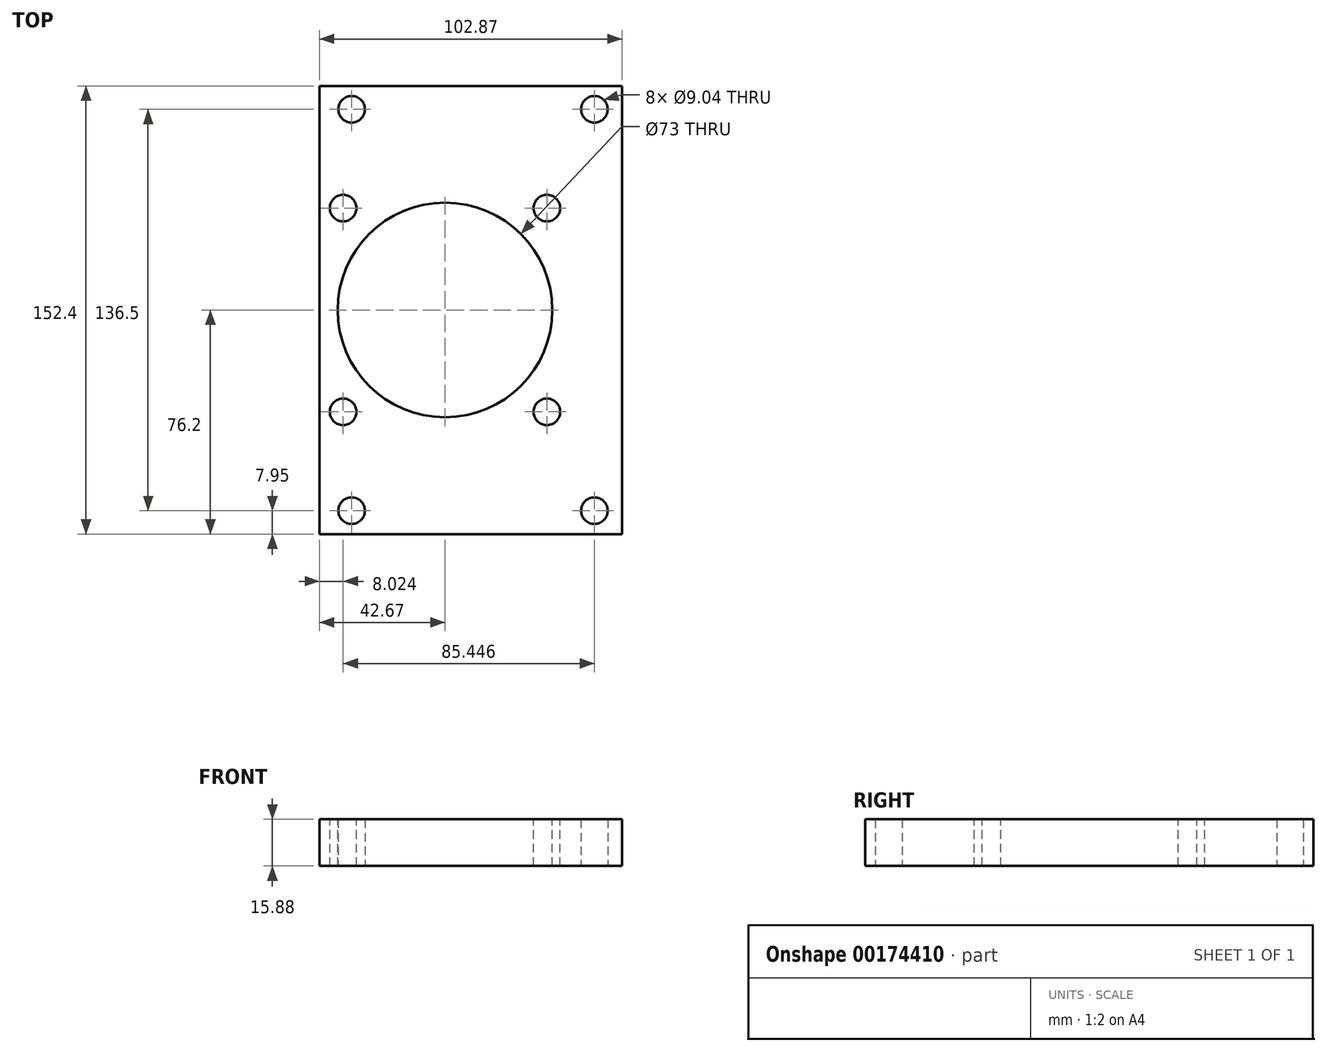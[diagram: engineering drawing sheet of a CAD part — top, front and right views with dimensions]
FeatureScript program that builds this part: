
annotation { "Feature Type Name" : "Feature", "Feature Type Description" : "" }
export const myFeature = defineFeature(function(context is Context, id is Id, definition is map)
    precondition{}
    {
        {
            var Q0;
            Q0=qCreatedBy(makeId("Top.planeOp"),FACE);
            var sketch = newSketch(context, id + "F0", { "sketchPlane" : qUnion([Q0])});
            skLineSegment(sketch, "E0.bottom", {"start": v(-42.67, 76.2) * mm, "end": v(60.2, 76.2) * mm});
            skLineSegment(sketch, "E0.top", {"start": v(-42.67, -76.2) * mm, "end": v(60.2, -76.2) * mm});
            skLineSegment(sketch, "E0.left", {"start": v(-42.67, 76.2) * mm, "end": v(-42.67, -76.2) * mm});
            skLineSegment(sketch, "E0.right", {"start": v(60.2, 76.2) * mm, "end": v(60.2, -76.2) * mm});
            skPoint(sketch, "E0.middle", {"position": v(8.76, 0) * mm});
            skCircle(sketch, "E1", {"center": v(-31.75, 68.25) * mm, "radius": 4.52 * mm});
            skCircle(sketch, "E2", {"center": v(50.8, 68.25) * mm, "radius": 4.52 * mm});
            skCircle(sketch, "E3", {"center": v(50.8, -68.25) * mm, "radius": 4.52 * mm});
            skCircle(sketch, "E4", {"center": v(-31.75, -68.25) * mm, "radius": 4.52 * mm});
            skSolve(sketch);
        }
        {
            var Q0;
            Q0=makeQuery(id+"F0.imprint","IMPRINT",FACE,{"disambiguationData":[TD([[makeQuery(id+"F0.imprint","IMPRINT",EDGE,{"derivedFrom":sQuery(id+"F0.wireOp",EDGE,"E0.bottom")}),-1.0]])]});
            extrude(context, id + "F1", {"entities" : qUnion([Q0]), "depth" : 15.88 * mm});
        }
        {
            var Q0;
            Q0 = qSketchRegion(id + "F0", true);
            extrude(context, id + "F2", {"entities" : qUnion([Q0]), "operationType" : NewBodyOperationType.REMOVE, "endBound" : BoundingType.THROUGH_ALL, "oppositeDirection" : true, "depth" : 25.4 * mm});
        }
        {
            var Q0;
            Q0=makeQuery(id+"F1.opExtrude","CAP_FACE",FACE,{"disambiguationData":[OSD([sQuery(id+"F0.wireOp",EDGE,"E0.bottom"),sQuery(id+"F0.wireOp",EDGE,"E0.top"),sQuery(id+"F0.wireOp",EDGE,"E0.left"),sQuery(id+"F0.wireOp",EDGE,"E0.right"),sQuery(id+"F0.wireOp",EDGE,"E1"),sQuery(id+"F0.wireOp",EDGE,"E2"),sQuery(id+"F0.wireOp",EDGE,"E3"),sQuery(id+"F0.wireOp",EDGE,"E4")])],"isStart":false});
            var sketch = newSketch(context, id + "F3", { "sketchPlane" : qUnion([Q0])});
            skCircle(sketch, "E5", {"center": v(0, 0) * mm, "radius": 36.5 * mm});
            skSolve(sketch);
        }
        {
            var Q0;
            Q0 = qSketchRegion(id + "F3", true);
            extrude(context, id + "F4", {"entities" : qUnion([Q0]), "operationType" : NewBodyOperationType.REMOVE, "endBound" : BoundingType.THROUGH_ALL, "oppositeDirection" : true, "depth" : 25.4 * mm});
        }
        {
            var Q0;
            Q0=makeQuery(id+"F1.opExtrude","CAP_FACE",FACE,{"disambiguationData":[OSD([sQuery(id+"F0.wireOp",EDGE,"E0.bottom"),sQuery(id+"F0.wireOp",EDGE,"E0.top"),sQuery(id+"F0.wireOp",EDGE,"E0.left"),sQuery(id+"F0.wireOp",EDGE,"E0.right"),sQuery(id+"F0.wireOp",EDGE,"E1"),sQuery(id+"F0.wireOp",EDGE,"E2"),sQuery(id+"F0.wireOp",EDGE,"E3"),sQuery(id+"F0.wireOp",EDGE,"E4")])],"isStart":false});
            var sketch = newSketch(context, id + "F5", { "sketchPlane" : qUnion([Q0])});
            skCircle(sketch, "E6", {"center": v(-34.65, 34.65) * mm, "radius": 4.52 * mm});
            skCircle(sketch, "E7", {"center": v(34.65, 34.65) * mm, "radius": 4.52 * mm});
            skCircle(sketch, "E8", {"center": v(34.65, -34.65) * mm, "radius": 4.52 * mm});
            skCircle(sketch, "E9", {"center": v(-34.65, -34.65) * mm, "radius": 4.52 * mm});
            skSolve(sketch);
        }
        {
            var Q0;
            Q0 = qSketchRegion(id + "F5", true);
            extrude(context, id + "F6", {"entities" : qUnion([Q0]), "operationType" : NewBodyOperationType.REMOVE, "endBound" : BoundingType.THROUGH_ALL, "oppositeDirection" : true, "depth" : 25.4 * mm});
        }
    });
